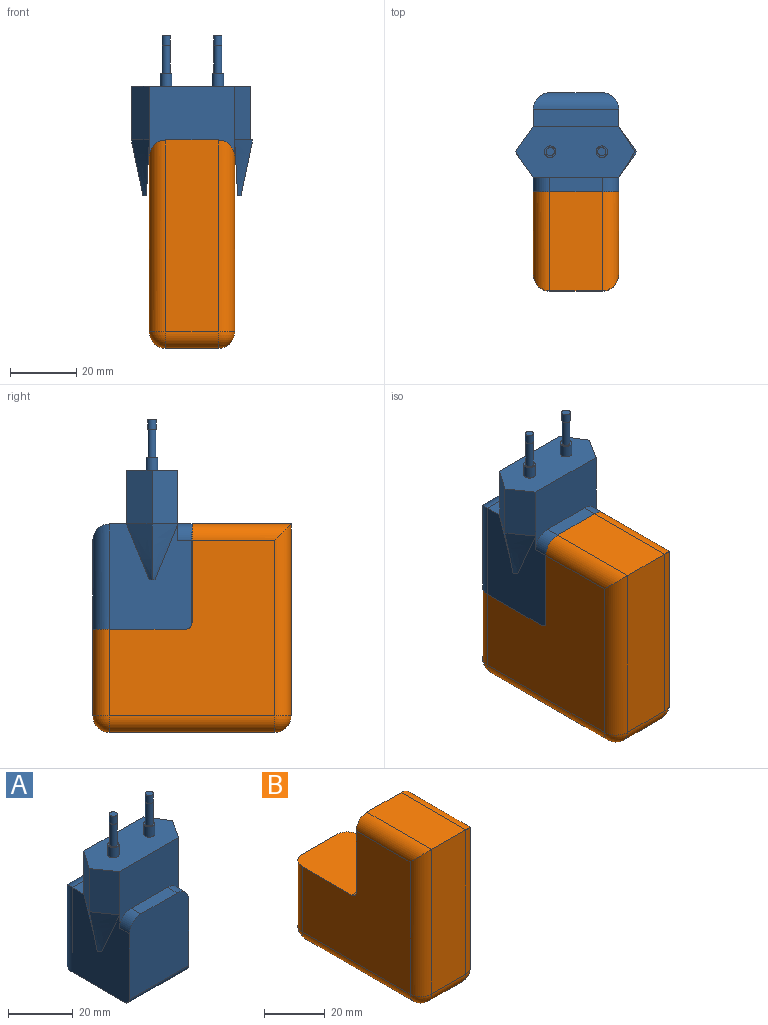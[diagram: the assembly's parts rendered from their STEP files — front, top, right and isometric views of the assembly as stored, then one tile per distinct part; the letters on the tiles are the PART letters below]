
ASSEMBLY  parts=2 mates=1
PART A: 41 faces, bbox 36.7x30x63.5 mm
  f0: plane 26.89x15.84mm, normal (0,1,0), area 426mm2, adj f1,f2,f21,f39
  f1: cylinder r=5mm len=31.89mm, axis (0,0,1), area 236.2mm2, adj f0,f4,f21,f39
  f2: cylinder r=5mm len=31.89mm, axis (0,0,-1), area 236.2mm2, adj f0,f5,f21,f39
  f3: plane 15.84x4.3mm, normal (0,0,1), area 68.1mm2, adj f8,f20,f22,f38
  f4: plane 31.89x25mm, normal (1,0,0), area 774.9mm2, adj f1,f6,f8,f20,f29,f38,f39,f40
  f5: plane 31.89x25mm, normal (-1,0,0), area 774.9mm2, adj f2,f6,f8,f22,f24,f38,f39,f40
  f6: plane 25.84x5.16mm, normal (0,0,1), area 133.5mm2, adj f4,f5,f11,f21
  f7: plane 16.3x7.77mm, normal (-0.82,-0.57,0), area 154.6mm2, adj f8,f12,f13,f25
  f8: plane 25.84x21.3mm, normal (0,-1,0), area 431.9mm2, adj f3,f4,f5,f7,f9,f13,f20,f22
  f9: plane 16.3x7.77mm, normal (0.85,-0.53,0), area 149.6mm2, adj f8,f10,f13,f27
  f10: plane 16.3x7.77mm, normal (0.85,0.53,0), area 149.6mm2, adj f9,f11,f13,f27
  f11: plane 25.84x16.3mm, normal (0,1,0), area 421.2mm2, adj f6,f10,f12,f13
  f12: plane 16.3x7.77mm, normal (-0.82,0.57,0), area 154.6mm2, adj f7,f11,f13,f26
  f13: plane 36.17x15.53mm, normal (0,0,1), area 462.5mm2, adj f7,f8,f9,f10,f11,f12,f14,f16
  f14: cylinder r=1.75mm len=3.9mm, axis (0,0,-1), area 42.8mm2, adj f13,f15
  f15: plane 3.5x3.5mm, normal (0,0,1), area 5.1mm2, adj f14,f18
  f16: cylinder r=1.75mm len=3.9mm, axis (0,0,-1), area 42.8mm2, adj f13,f17
  f17: plane 3.5x3.5mm, normal (0,0,1), area 5.1mm2, adj f16,f19
  f18: cylinder r=1.2mm len=8.4mm, axis (0,0,-1), area 63.3mm2, adj f15,f34
  f19: cylinder r=1.2mm len=8.4mm, axis (0,0,-1), area 63.3mm2, adj f17,f37
  f20: cylinder r=5mm len=5mm, axis (0,-1,0), area 33.8mm2, adj f3,f4,f8,f38
  f21: cylinder r=5mm len=25.84mm, axis (1,0,0), area 174.4mm2, adj f0,f1,f2,f6
  f22: cylinder r=5mm len=5mm, axis (0,1,0), area 33.8mm2, adj f3,f5,f8,f38
  f23: plane 1.75x1.03mm, normal (0,0,-1), area 0.9mm2, adj f24,f25,f26
  f24: bspline ~16.9x15.53mm, area 146.3mm2, adj f5,f23,f25,f26
  f25: bspline ~16.9x7.77mm, area 92.9mm2, adj f7,f23,f24,f26
  f26: bspline ~16.9x7.77mm, area 92.5mm2, adj f12,f23,f24,f25
  f27: plane 15.53x5.44mm, normal (0,0,1), area 4.3mm2, adj f9,f10,f30,f31
  f28: plane 1.75x1.03mm, normal (0,0,-1), area 0.9mm2, adj f29,f30,f31
  f29: bspline ~16.9x15.53mm, area 146.3mm2, adj f4,f28,f30,f31
  f30: bspline ~16.9x7.77mm, area 92.9mm2, adj f27,f28,f29,f31
  f31: bspline ~16.9x7.77mm, area 92.5mm2, adj f27,f28,f29,f30
  f32: cylinder r=1.25mm len=3mm, axis (0,0,-1), area 23.6mm2, adj f33,f34
  f33: plane 2.5x2.5mm, normal (0,0,1), area 4.9mm2, adj f32
  f34: plane 2.5x2.5mm, normal (0,0,-1), area 0.4mm2, adj f18,f32
  f35: cylinder r=1.25mm len=3mm, axis (0,0,-1), area 23.6mm2, adj f36,f37
  f36: plane 2.5x2.5mm, normal (0,0,1), area 4.9mm2, adj f35
  f37: plane 2.5x2.5mm, normal (0,0,-1), area 0.4mm2, adj f19,f35
  f38: plane 29.89x25.84mm, normal (0,-1,0), area 761.7mm2, adj f3,f4,f5,f20,f22,f40
  f39: plane 28x25.84mm, normal (0,0,-1), area 712.8mm2, adj f0,f1,f2,f4,f5,f40
  f40: cylinder r=2mm len=25.84mm, axis (1,0,0), area 81.2mm2, adj f4,f5,f38,f39
PART B: 33 faces, bbox 25.8x60x63.1 mm
  f0: plane 26.21x15.84mm, normal (0,1,0), area 415.2mm2, adj f1,f2,f12,f31
  f1: cylinder r=5mm len=26.21mm, axis (0,0,1), area 205.8mm2, adj f0,f6,f9,f31
  f2: cylinder r=5mm len=26.21mm, axis (0,0,-1), area 205.8mm2, adj f0,f7,f14,f31
  f3: plane 50x15.84mm, normal (0,0,-1), area 721.9mm2, adj f11,f12,f15,f16,f23,f24,f25,f26
  f4: plane 30x15.84mm, normal (0,0,1), area 475.2mm2, adj f5,f8,f19,f30
  f5: plane 58.1x15.84mm, normal (0,-1,0), area 920.4mm2, adj f4,f10,f15,f18
  f6: plane 53.1x50mm, normal (1,0,0), area 1983.6mm2, adj f1,f8,f10,f11,f30,f31,f32
  f7: plane 53.1x50mm, normal (-1,0,0), area 1983.6mm2, adj f2,f16,f18,f19,f30,f31,f32
  f8: cylinder r=5mm len=30mm, axis (0,-1,0), area 221.3mm2, adj f4,f6,f10,f30
  f9: sphere r=5mm, area 39.3mm2, adj f1,f11,f12
  f10: cylinder r=5mm len=58.1mm, axis (0,0,-1), area 442mm2, adj f5,f6,f8,f13
  f11: cylinder r=5mm len=50mm, axis (0,1,0), area 392.7mm2, adj f3,f6,f9,f13
  f12: cylinder r=5mm len=15.84mm, axis (-1,0,0), area 124.4mm2, adj f0,f3,f9,f14
  f13: sphere r=5mm, area 39.3mm2, adj f10,f11,f15
  f14: sphere r=5mm, area 39.3mm2, adj f2,f12,f16
  f15: cylinder r=5mm len=15.84mm, axis (1,0,0), area 124.4mm2, adj f3,f5,f13,f17
  f16: cylinder r=5mm len=50mm, axis (0,-1,0), area 392.7mm2, adj f3,f7,f14,f17
  f17: sphere r=5mm, area 39.3mm2, adj f15,f16,f18
  f18: cylinder r=5mm len=58.1mm, axis (0,0,1), area 442mm2, adj f5,f7,f17,f19
  f19: cylinder r=5mm len=30mm, axis (0,1,0), area 221.3mm2, adj f4,f7,f18,f30
  f20: plane 8.3x1.71mm, normal (1,0,0), area 14.2mm2, adj f21,f27,f28,f29
  f21: plane 8.3x5.86mm, normal (0,1,0), area 48.6mm2, adj f20,f22,f28,f29
  f22: plane 8.3x1.71mm, normal (-1,0,0), area 14.2mm2, adj f21,f27,f28,f29
  f23: plane 8.3x6.69mm, normal (-1,0,0), area 55.5mm2, adj f3,f24,f26,f28
  f24: plane 10.49x8.3mm, normal (0,1,0), area 87mm2, adj f3,f23,f25,f28
  f25: plane 8.3x6.69mm, normal (1,0,0), area 55.5mm2, adj f3,f24,f26,f28
  f26: plane 10.49x8.3mm, normal (0,-1,0), area 87mm2, adj f3,f23,f25,f28
  f27: plane 8.3x5.86mm, normal (0,-1,0), area 48.6mm2, adj f20,f22,f28,f29
  f28: plane 10.49x6.69mm, normal (0,0,-1), area 60.1mm2, adj f20,f21,f22,f23,f24,f25,f26,f27
  f29: plane 5.86x1.71mm, normal (0,0,-1), area 10mm2, adj f20,f21,f22,f27
  f30: plane 29.89x25.84mm, normal (0,1,0), area 761.7mm2, adj f4,f6,f7,f8,f19,f32
  f31: plane 28x25.84mm, normal (0,0,1), area 712.8mm2, adj f0,f1,f2,f6,f7,f32
  f32: cylinder r=2mm len=25.84mm, axis (-1,0,0), area 81.2mm2, adj f6,f7,f30,f31
PLACE A t=(-2.53,-25.61,5.27)mm
PLACE B t=(-2.53,-25.61,5.27)mm fixed
MATE planar A.f39 <-> B.f31  axis (0,0,-1) through (-2.53,-9.81,6.28)mm
